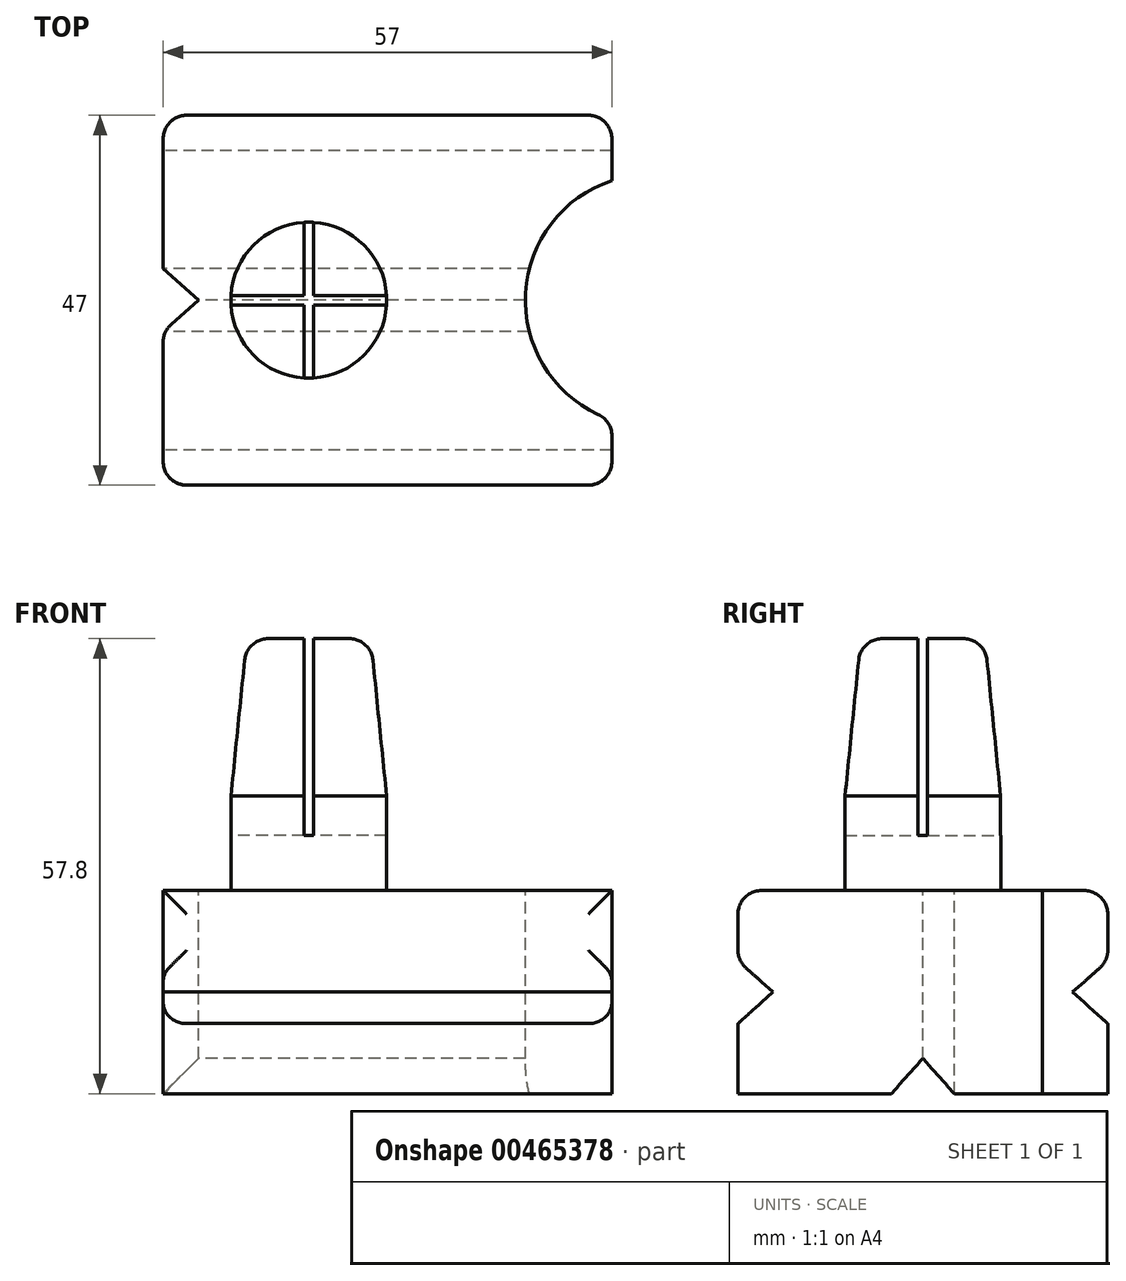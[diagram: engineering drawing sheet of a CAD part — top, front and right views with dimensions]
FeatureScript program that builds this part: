
annotation { "Feature Type Name" : "Feature", "Feature Type Description" : "" }
export const myFeature = defineFeature(function(context is Context, id is Id, definition is map)
    precondition{}
    {
        {
            var Q0;
            Q0=qCreatedBy(makeId("Top.planeOp"),FACE);
            var sketch = newSketch(context, id + "F0", { "sketchPlane" : qUnion([Q0])});
            skLineSegment(sketch, "E0.bottom", {"start": v(18.5, -23.5) * mm, "end": v(-18.5, -23.5) * mm});
            skLineSegment(sketch, "E0.top", {"start": v(18.5, 23.5) * mm, "end": v(-18.5, 23.5) * mm});
            skLineSegment(sketch, "E0.left", {"start": v(18.5, -23.5) * mm, "end": v(18.5, 23.5) * mm});
            skLineSegment(sketch, "E0.right", {"start": v(-18.5, -23.5) * mm, "end": v(-18.5, 23.5) * mm});
            skPoint(sketch, "E0.middle", {"position": v(0, 0) * mm});
            skCircle(sketch, "E1", {"center": v(0, 0) * mm, "radius": 9.9 * mm});
            skSolve(sketch);
        }
        {
            var Q0;
            Q0=makeQuery(id+"F0.imprint","IMPRINT",FACE,{"disambiguationData":[TD([[makeQuery(id+"F0.imprint","IMPRINT",EDGE,{"derivedFrom":sQuery(id+"F0.wireOp",EDGE,"E1")}),1.0]])]});
            extrude(context, id + "F1", {"entities" : qUnion([Q0]), "depth" : 32 * mm});
        }
        {
            var Q0;
            Q0=makeQuery(id+"F0.imprint","IMPRINT",FACE,{"disambiguationData":[TD([[makeQuery(id+"F0.imprint","IMPRINT",EDGE,{"derivedFrom":sQuery(id+"F0.wireOp",EDGE,"E0.bottom")}),-1.0]])]});
            var Q1;
            Q1=makeQuery(id+"F0.imprint","IMPRINT",FACE,{"disambiguationData":[TD([[makeQuery(id+"F0.imprint","IMPRINT",EDGE,{"derivedFrom":sQuery(id+"F0.wireOp",EDGE,"E1")}),1.0]])]});
            extrude(context, id + "F2", {"entities" : qUnion([Q0, Q1]), "operationType" : NewBodyOperationType.ADD, "oppositeDirection" : true, "depth" : 25.8 * mm});
        }
        {
            var Q0;
            Q0=makeQuery(id+"F2.opExtrude","SWEPT_FACE",FACE,{"disambiguationData":[OSD([sQuery(id+"F0.wireOp",EDGE,"E0.left")])]});
            extrude(context, id + "F3", {"entities" : qUnion([Q0]), "operationType" : NewBodyOperationType.ADD, "depth" : 20 * mm});
        }
        {
            var Q0;
            {var subQ0=sQuery(id+"F0.wireOp",EDGE,"E0.left");Q0=makeQuery(id+"F3.boolean.opBoolean","MERGE",FACE,{"derivedFrom":[makeQuery(id+"F2.opExtrude","CAP_FACE",FACE,{"disambiguationData":[OSD([sQuery(id+"F0.wireOp",EDGE,"E0.bottom"),sQuery(id+"F0.wireOp",EDGE,"E0.top"),subQ0,sQuery(id+"F0.wireOp",EDGE,"E0.right")])],"isStart":true}),makeQuery(id+"F3.opExtrude","SWEPT_FACE",FACE,{"disambiguationData":[OSD([subQ0]),TDD([makeQuery(id+"F2.opExtrude","CAP_EDGE",EDGE,{"disambiguationData":[OSD([subQ0])],"isStart":true})])]})]});}
            var sketch = newSketch(context, id + "F4", { "sketchPlane" : qUnion([Q0])});
            skCircle(sketch, "E2", {"center": v(43.5, 0) * mm, "radius": 16 * mm});
            skSolve(sketch);
        }
        {
            var Q0;
            Q0=makeQuery(id+"F1.opExtrude","CAP_EDGE",EDGE,{"disambiguationData":[OSD([sQuery(id+"F0.wireOp",EDGE,"E1")])],"isStart":false});
            chamfer(context, id + "F5", {"entities" : qUnion([Q0]), "chamferType" : ChamferType.TWO_OFFSETS, "width1" : 2 * mm, "oppositeDirection" : false, "width2" : 20 * mm, "tangentPropagation" : true});
        }
        {
            var Q0;
            {var subQ0=sQuery(id+"F4.wireOp",EDGE,"E2");var subQ1=sQuery(id+"F0.wireOp",EDGE,"E0.left");var subQ2=makeQuery(id+"F3.opExtrude","CAP_EDGE",EDGE,{"disambiguationData":[OSD([subQ1]),TDD([makeQuery(id+"F2.opExtrude","CAP_EDGE",EDGE,{"disambiguationData":[OSD([subQ1])],"isStart":true})])],"isStart":false});var subQ3=makeQuery(id+"F4.imprint","INTERSECT",VERTEX,{"disambiguationData":[OD(0.0)],"derivedFrom":[subQ2,subQ0]});Q0=makeQuery(id+"F4.imprint","IMPRINT",FACE,{"disambiguationData":[TD([[makeQuery(id+"F4.imprint","IMPRINT",EDGE,{"disambiguationData":[TD([[subQ3,1.0]])],"derivedFrom":subQ0}),1.0]])]});}
            extrude(context, id + "F6", {"entities" : qUnion([Q0]), "operationType" : NewBodyOperationType.REMOVE, "endBound" : BoundingType.THROUGH_ALL, "oppositeDirection" : true, "depth" : 25 * mm});
        }
        {
            var Q0;
            {var subQ1=sQuery(id+"F0.wireOp",EDGE,"E0.top");var subQ2=sQuery(id+"F0.wireOp",EDGE,"E0.right");Q0=makeQuery(id+"FCS6urC5TY2NgVd_1.boolean.opBoolean","SPLIT",FACE,{"disambiguationData":[TD([makeQuery(id+"F2.opExtrude","SWEPT_FACE",FACE,{"disambiguationData":[OSD([subQ1])]})])],"derivedFrom":makeQuery(id+"F2.opExtrude","SWEPT_FACE",FACE,{"disambiguationData":[OSD([subQ2])]})});}
            var sketch = newSketch(context, id + "F7", { "sketchPlane" : qUnion([Q0])});
            skLineSegment(sketch, "E3", {"start": v(-23.5, -12.9) * mm, "end": v(23.5, -12.9) * mm, "construction": true});
            skLineSegment(sketch, "E4", {"start": v(-19.03, -12.9) * mm, "end": v(-23.5, -16.9) * mm});
            skLineSegment(sketch, "E5", {"start": v(-23.5, -16.9) * mm, "end": v(-23.5, -8.9) * mm});
            skLineSegment(sketch, "E6", {"start": v(-23.5, -8.9) * mm, "end": v(-19.03, -12.9) * mm});
            skLineSegment(sketch, "E7.MirrorCS", {"start": v(23.5, -16.9) * mm, "end": v(23.5, -8.9) * mm});
            skLineSegment(sketch, "E8.MirrorCS", {"start": v(23.5, -8.9) * mm, "end": v(19.03, -12.9) * mm});
            skLineSegment(sketch, "E9.MirrorCS", {"start": v(19.03, -12.9) * mm, "end": v(23.5, -16.9) * mm});
            skSolve(sketch);
        }
        {
            var Q0;
            Q0=makeQuery(id+"F7.imprint","IMPRINT",FACE,{"disambiguationData":[TD([[makeQuery(id+"F7.imprint","IMPRINT",EDGE,{"derivedFrom":sQuery(id+"F7.wireOp",EDGE,"E4")}),-1.0]])]});
            var Q1;
            Q1=makeQuery(id+"F7.imprint","IMPRINT",FACE,{"disambiguationData":[TD([[makeQuery(id+"F7.imprint","IMPRINT",EDGE,{"derivedFrom":sQuery(id+"F7.wireOp",EDGE,"E7.MirrorCS")}),1.0]])]});
            extrude(context, id + "F8", {"entities" : qUnion([Q0, Q1]), "operationType" : NewBodyOperationType.REMOVE, "endBound" : BoundingType.THROUGH_ALL, "oppositeDirection" : true, "depth" : 25 * mm});
        }
        {
            var Q0;
            Q0=makeQuery(id+"F0.imprint","IMPRINT",FACE,{"disambiguationData":[TD([[makeQuery(id+"F0.imprint","IMPRINT",EDGE,{"derivedFrom":sQuery(id+"F0.wireOp",EDGE,"E0.bottom")}),-1.0]])]});
            var sketch = newSketch(context, id + "F9", { "sketchPlane" : qUnion([Q0])});
            skLineSegment(sketch, "E10", {"start": v(-14.03, 0) * mm, "end": v(-18.5, 4) * mm});
            skLineSegment(sketch, "E11", {"start": v(-18.5, 4) * mm, "end": v(-18.5, -4) * mm});
            skLineSegment(sketch, "E12", {"start": v(-18.5, -4) * mm, "end": v(-14.03, 0) * mm});
            skSolve(sketch);
        }
        {
            var Q0;
            Q0=makeQuery(id+"F2.opExtrude","SWEPT_FACE",FACE,{"disambiguationData":[OSD([sQuery(id+"F0.wireOp",EDGE,"E0.right")])]});
            var sketch = newSketch(context, id + "F10", { "sketchPlane" : qUnion([Q0])});
            skLineSegment(sketch, "E13", {"start": v(0, -21.33) * mm, "end": v(-4, -25.8) * mm});
            skLineSegment(sketch, "E14", {"start": v(-4, -25.8) * mm, "end": v(4, -25.8) * mm});
            skLineSegment(sketch, "E15", {"start": v(4, -25.8) * mm, "end": v(0, -21.33) * mm});
            skSolve(sketch);
        }
        {
            var Q0;
            Q0=qSketchRegion(id+"F10",true);
            extrude(context, id + "F11", {"entities" : qUnion([Q0]), "operationType" : NewBodyOperationType.REMOVE, "endBound" : BoundingType.THROUGH_ALL, "oppositeDirection" : true, "depth" : 25 * mm});
        }
        {
            var Q0;
            Q0=makeQuery(id+"F9.imprint","IMPRINT",FACE,{"disambiguationData":[TD([[makeQuery(id+"F9.imprint","IMPRINT",EDGE,{"derivedFrom":sQuery(id+"F9.wireOp",EDGE,"E10")}),1.0]])]});
            extrude(context, id + "F12", {"entities" : qUnion([Q0]), "operationType" : NewBodyOperationType.REMOVE, "endBound" : BoundingType.THROUGH_ALL, "oppositeDirection" : true, "depth" : 25 * mm});
        }
        {
            var Q0;
            Q0=makeQuery(id+"F1.opExtrude","CAP_FACE",FACE,{"disambiguationData":[OSD([sQuery(id+"F0.wireOp",EDGE,"E1")])],"isStart":false});
            var sketch = newSketch(context, id + "F13", { "sketchPlane" : qUnion([Q0])});
            skLineSegment(sketch, "E16.bottom", {"start": v(0.6, -10.5) * mm, "end": v(-0.6, -10.5) * mm});
            skLineSegment(sketch, "E16.top", {"start": v(0.6, 10.5) * mm, "end": v(-0.6, 10.5) * mm});
            skLineSegment(sketch, "E16.left", {"start": v(0.6, -10.5) * mm, "end": v(0.6, 10.5) * mm});
            skLineSegment(sketch, "E16.right", {"start": v(-0.6, -10.5) * mm, "end": v(-0.6, 10.5) * mm});
            skPoint(sketch, "E16.middle", {"position": v(0, 0) * mm});
            skLineSegment(sketch, "E17.bottom", {"start": v(10.5, -0.6) * mm, "end": v(-10.5, -0.6) * mm});
            skLineSegment(sketch, "E17.top", {"start": v(10.5, 0.6) * mm, "end": v(-10.5, 0.6) * mm});
            skLineSegment(sketch, "E17.left", {"start": v(10.5, -0.6) * mm, "end": v(10.5, 0.6) * mm});
            skLineSegment(sketch, "E17.right", {"start": v(-10.5, -0.6) * mm, "end": v(-10.5, 0.6) * mm});
            skSolve(sketch);
        }
        {
            var Q0;
            Q0=qSketchRegion(id+"F13",true);
            extrude(context, id + "F14", {"entities" : qUnion([Q0]), "operationType" : NewBodyOperationType.REMOVE, "oppositeDirection" : true, "depth" : 25 * mm});
        }
        {
            var Q0;
            {var subQ0=sQuery(id+"F0.wireOp",EDGE,"E0.right");var subQ2=sQuery(id+"F0.wireOp",EDGE,"E0.top");Q0=makeQuery(id+"F8.boolean.opBoolean","SPLIT",EDGE,{"disambiguationData":[TD([makeQuery(id+"F8.opExtrude","SWEPT_FACE",FACE,{"disambiguationData":[OSD([sQuery(id+"F7.wireOp",EDGE,"E6")])]})])],"derivedFrom":makeQuery(id+"F2.opExtrude","SWEPT_EDGE",EDGE,{"disambiguationData":[OSD([subQ2,subQ0])]})});}
            var Q1;
            {var subQ0=sQuery(id+"F0.wireOp",EDGE,"E0.right");var subQ2=sQuery(id+"F0.wireOp",EDGE,"E0.top");Q1=makeQuery(id+"F8.boolean.opBoolean","SPLIT",EDGE,{"disambiguationData":[TD([makeQuery(id+"F8.opExtrude","SWEPT_FACE",FACE,{"disambiguationData":[OSD([sQuery(id+"F7.wireOp",EDGE,"E4")])]})])],"derivedFrom":makeQuery(id+"F2.opExtrude","SWEPT_EDGE",EDGE,{"disambiguationData":[OSD([subQ2,subQ0])]})});}
            var Q2;
            {var subQ1=sQuery(id+"F0.wireOp",EDGE,"E0.bottom");var subQ2=sQuery(id+"F0.wireOp",EDGE,"E0.right");Q2=makeQuery(id+"F8.boolean.opBoolean","SPLIT",EDGE,{"disambiguationData":[TD([makeQuery(id+"F8.opExtrude","SWEPT_FACE",FACE,{"disambiguationData":[OSD([sQuery(id+"F7.wireOp",EDGE,"E8.MirrorCS")])]})])],"derivedFrom":makeQuery(id+"F2.opExtrude","SWEPT_EDGE",EDGE,{"disambiguationData":[OSD([subQ1,subQ2])]})});}
            var Q3;
            {var subQ1=sQuery(id+"F0.wireOp",EDGE,"E0.bottom");var subQ2=sQuery(id+"F0.wireOp",EDGE,"E0.right");Q3=makeQuery(id+"F8.boolean.opBoolean","SPLIT",EDGE,{"disambiguationData":[TD([makeQuery(id+"F8.opExtrude","SWEPT_FACE",FACE,{"disambiguationData":[OSD([sQuery(id+"F7.wireOp",EDGE,"E9.MirrorCS")])]})])],"derivedFrom":makeQuery(id+"F2.opExtrude","SWEPT_EDGE",EDGE,{"disambiguationData":[OSD([subQ1,subQ2])]})});}
            var Q4;
            {var subQ0=sQuery(id+"F0.wireOp",EDGE,"E0.left");var subQ1=sQuery(id+"F0.wireOp",EDGE,"E0.bottom");Q4=makeQuery(id+"F8.boolean.opBoolean","SPLIT",EDGE,{"disambiguationData":[TD([makeQuery(id+"F8.opExtrude","SWEPT_FACE",FACE,{"disambiguationData":[OSD([sQuery(id+"F7.wireOp",EDGE,"E8.MirrorCS")])]})])],"derivedFrom":makeQuery(id+"F3.opExtrude","CAP_EDGE",EDGE,{"disambiguationData":[OSD([subQ1,subQ0])],"isStart":false})});}
            var Q5;
            {var subQ0=sQuery(id+"F0.wireOp",EDGE,"E0.left");var subQ1=sQuery(id+"F0.wireOp",EDGE,"E0.bottom");Q5=makeQuery(id+"F8.boolean.opBoolean","SPLIT",EDGE,{"disambiguationData":[TD([makeQuery(id+"F8.opExtrude","SWEPT_FACE",FACE,{"disambiguationData":[OSD([sQuery(id+"F7.wireOp",EDGE,"E9.MirrorCS")])]})])],"derivedFrom":makeQuery(id+"F3.opExtrude","CAP_EDGE",EDGE,{"disambiguationData":[OSD([subQ1,subQ0])],"isStart":false})});}
            var Q6;
            {var subQ0=sQuery(id+"F4.wireOp",EDGE,"E2");var subQ1=sQuery(id+"F0.wireOp",EDGE,"E0.left");Q6=makeQuery(id+"F6.boolean.opBoolean","COPY",EDGE,{"derivedFrom":makeQuery(id+"F6.opExtrude","SWEPT_EDGE",EDGE,{"disambiguationData":[OSD([subQ1,subQ0]),TDD([makeQuery(id+"F4.imprint","INTERSECT",VERTEX,{"disambiguationData":[OD(1.0)],"derivedFrom":[makeQuery(id+"F3.opExtrude","CAP_EDGE",EDGE,{"disambiguationData":[OSD([subQ1]),TDD([makeQuery(id+"F2.opExtrude","CAP_EDGE",EDGE,{"disambiguationData":[OSD([subQ1])],"isStart":true})])],"isStart":false}),subQ0]})])]})});}
            var Q7;
            {var subQ0=sQuery(id+"F4.wireOp",EDGE,"E2");var subQ1=sQuery(id+"F0.wireOp",EDGE,"E0.left");Q7=makeQuery(id+"F6.boolean.opBoolean","COPY",EDGE,{"derivedFrom":makeQuery(id+"F6.opExtrude","SWEPT_EDGE",EDGE,{"disambiguationData":[OSD([subQ1,subQ0]),TDD([makeQuery(id+"F4.imprint","INTERSECT",VERTEX,{"disambiguationData":[OD(0.0)],"derivedFrom":[makeQuery(id+"F3.opExtrude","CAP_EDGE",EDGE,{"disambiguationData":[OSD([subQ1]),TDD([makeQuery(id+"F2.opExtrude","CAP_EDGE",EDGE,{"disambiguationData":[OSD([subQ1])],"isStart":true})])],"isStart":false}),subQ0]})])]})});}
            var Q8;
            {var subQ0=sQuery(id+"F0.wireOp",EDGE,"E0.left");var subQ1=sQuery(id+"F0.wireOp",EDGE,"E0.top");Q8=makeQuery(id+"F8.boolean.opBoolean","SPLIT",EDGE,{"disambiguationData":[TD([makeQuery(id+"F8.opExtrude","SWEPT_FACE",FACE,{"disambiguationData":[OSD([sQuery(id+"F7.wireOp",EDGE,"E6")])]})])],"derivedFrom":makeQuery(id+"F3.opExtrude","CAP_EDGE",EDGE,{"disambiguationData":[OSD([subQ1,subQ0])],"isStart":false})});}
            var Q9;
            {var subQ0=sQuery(id+"F0.wireOp",EDGE,"E0.left");var subQ1=sQuery(id+"F0.wireOp",EDGE,"E0.top");Q9=makeQuery(id+"F8.boolean.opBoolean","SPLIT",EDGE,{"disambiguationData":[TD([makeQuery(id+"F8.opExtrude","SWEPT_FACE",FACE,{"disambiguationData":[OSD([sQuery(id+"F7.wireOp",EDGE,"E4")])]})])],"derivedFrom":makeQuery(id+"F3.opExtrude","CAP_EDGE",EDGE,{"disambiguationData":[OSD([subQ1,subQ0])],"isStart":false})});}
            var Q10;
            {var subQ0=sQuery(id+"F0.wireOp",EDGE,"E0.left");var subQ1=sQuery(id+"F0.wireOp",EDGE,"E0.bottom");Q10=makeQuery(id+"F3.boolean.opBoolean","MERGE",EDGE,{"derivedFrom":[makeQuery(id+"F2.opExtrude","CAP_EDGE",EDGE,{"disambiguationData":[OSD([subQ1])],"isStart":true}),makeQuery(id+"F3.opExtrude","SWEPT_EDGE",EDGE,{"disambiguationData":[OSD([subQ1,subQ0]),TDD([makeQuery(id+"F2.opExtrude","CAP_VERTEX",VERTEX,{"disambiguationData":[OSD([subQ1,subQ0])],"isStart":true})])]})]});}
            var Q11;
            {var subQ0=sQuery(id+"F0.wireOp",EDGE,"E0.left");var subQ1=sQuery(id+"F0.wireOp",EDGE,"E0.top");Q11=makeQuery(id+"F3.boolean.opBoolean","MERGE",EDGE,{"derivedFrom":[makeQuery(id+"F2.opExtrude","CAP_EDGE",EDGE,{"disambiguationData":[OSD([subQ1])],"isStart":true}),makeQuery(id+"F3.opExtrude","SWEPT_EDGE",EDGE,{"disambiguationData":[OSD([subQ1,subQ0]),TDD([makeQuery(id+"F2.opExtrude","CAP_VERTEX",VERTEX,{"disambiguationData":[OSD([subQ1,subQ0])],"isStart":true})])]})]});}
            var Q12;
            Q12=makeQuery(id+"F8.boolean.opBoolean","COPY",EDGE,{"derivedFrom":makeQuery(id+"F8.opExtrude","SWEPT_EDGE",EDGE,{"disambiguationData":[OSD([sQuery(id+"F0.wireOp",EDGE,"E0.top"),sQuery(id+"F0.wireOp",EDGE,"E0.right"),sQuery(id+"F7.wireOp",EDGE,"E4"),sQuery(id+"F7.wireOp",EDGE,"E5")])]})});
            var Q13;
            Q13=makeQuery(id+"F8.boolean.opBoolean","COPY",EDGE,{"derivedFrom":makeQuery(id+"F8.opExtrude","SWEPT_EDGE",EDGE,{"disambiguationData":[OSD([sQuery(id+"F0.wireOp",EDGE,"E0.bottom"),sQuery(id+"F0.wireOp",EDGE,"E0.right"),sQuery(id+"F7.wireOp",EDGE,"E7.MirrorCS"),sQuery(id+"F7.wireOp",EDGE,"E8.MirrorCS")])]})});
            var Q14;
            Q14=makeQuery(id+"F8.boolean.opBoolean","COPY",EDGE,{"derivedFrom":makeQuery(id+"F8.opExtrude","SWEPT_EDGE",EDGE,{"disambiguationData":[OSD([sQuery(id+"F0.wireOp",EDGE,"E0.bottom"),sQuery(id+"F0.wireOp",EDGE,"E0.right"),sQuery(id+"F7.wireOp",EDGE,"E7.MirrorCS"),sQuery(id+"F7.wireOp",EDGE,"E9.MirrorCS")])]})});
            var Q15;
            Q15=makeQuery(id+"F8.boolean.opBoolean","COPY",EDGE,{"derivedFrom":makeQuery(id+"F8.opExtrude","SWEPT_EDGE",EDGE,{"disambiguationData":[OSD([sQuery(id+"F0.wireOp",EDGE,"E0.top"),sQuery(id+"F0.wireOp",EDGE,"E0.right"),sQuery(id+"F7.wireOp",EDGE,"E5"),sQuery(id+"F7.wireOp",EDGE,"E6")])]})});
            var Q16;
            Q16=makeQuery(id+"F12.boolean.opBoolean","COPY",EDGE,{"derivedFrom":makeQuery(id+"F12.opExtrude","SWEPT_EDGE",EDGE,{"disambiguationData":[OSD([sQuery(id+"F0.wireOp",EDGE,"E0.right"),sQuery(id+"F9.wireOp",EDGE,"E10"),sQuery(id+"F9.wireOp",EDGE,"E11")])]})});
            var Q17;
            Q17=makeQuery(id+"F12.boolean.opBoolean","COPY",EDGE,{"derivedFrom":makeQuery(id+"F12.opExtrude","SWEPT_EDGE",EDGE,{"disambiguationData":[OSD([sQuery(id+"F0.wireOp",EDGE,"E0.right"),sQuery(id+"F9.wireOp",EDGE,"E11"),sQuery(id+"F9.wireOp",EDGE,"E12")])]})});
            var Q18;
            {var subQ0=sQuery(id+"F0.wireOp",EDGE,"E1");var subQ1=makeQuery(id+"F1.opExtrude","CAP_FACE",FACE,{"disambiguationData":[OSD([subQ0])],"isStart":false});var subQ2=sQuery(id+"F13.wireOp",EDGE,"E16.right");var subQ3=makeQuery(id+"F5.opChamfer","BLEND_EDGE",EDGE,{"blendedFrom":[makeQuery(id+"F1.opExtrude","CAP_EDGE",EDGE,{"disambiguationData":[OSD([subQ0])],"isStart":false}),subQ1],"blendedInto":[subQ1]});var subQ5=sQuery(id+"F13.wireOp",EDGE,"E17.top");var subQ6=makeQuery(id+"F13.imprint","INTERSECT",VERTEX,{"derivedFrom":[subQ2,subQ5]});Q18=makeQuery(id+"F14.boolean.opBoolean","SPLIT",EDGE,{"disambiguationData":[TD([makeQuery(id+"F14.opExtrude","SWEPT_FACE",FACE,{"disambiguationData":[OSD([subQ2]),TDD([makeQuery(id+"F13.imprint","IMPRINT",EDGE,{"disambiguationData":[TD([[subQ6,-1.0]])],"derivedFrom":subQ2}),makeQuery(id+"F13.imprint","IMPRINT",EDGE,{"disambiguationData":[TD([[makeQuery(id+"F13.imprint","INTERSECT",VERTEX,{"derivedFrom":[sQuery(id+"F13.wireOp",EDGE,"E16.top"),subQ2]}),1.0]])],"derivedFrom":subQ2})])]})])],"derivedFrom":subQ3});}
            var Q19;
            {var subQ0=sQuery(id+"F0.wireOp",EDGE,"E1");var subQ1=makeQuery(id+"F1.opExtrude","CAP_FACE",FACE,{"disambiguationData":[OSD([subQ0])],"isStart":false});var subQ2=sQuery(id+"F13.wireOp",EDGE,"E17.bottom");var subQ3=sQuery(id+"F13.wireOp",EDGE,"E16.right");var subQ4=makeQuery(id+"F13.imprint","INTERSECT",VERTEX,{"derivedFrom":[subQ3,subQ2]});var subQ5=makeQuery(id+"F5.opChamfer","BLEND_EDGE",EDGE,{"blendedFrom":[makeQuery(id+"F1.opExtrude","CAP_EDGE",EDGE,{"disambiguationData":[OSD([subQ0])],"isStart":false}),subQ1],"blendedInto":[subQ1]});Q19=makeQuery(id+"F14.boolean.opBoolean","SPLIT",EDGE,{"disambiguationData":[TD([makeQuery(id+"F14.opExtrude","SWEPT_FACE",FACE,{"disambiguationData":[OSD([subQ3]),TDD([makeQuery(id+"F13.imprint","IMPRINT",EDGE,{"disambiguationData":[TD([[makeQuery(id+"F13.imprint","INTERSECT",VERTEX,{"derivedFrom":[sQuery(id+"F13.wireOp",EDGE,"E16.bottom"),subQ3]}),-1.0]])],"derivedFrom":subQ3}),makeQuery(id+"F13.imprint","IMPRINT",EDGE,{"disambiguationData":[TD([[subQ4,1.0]])],"derivedFrom":subQ3})])]})])],"derivedFrom":subQ5});}
            var Q20;
            {var subQ0=sQuery(id+"F0.wireOp",EDGE,"E1");var subQ1=makeQuery(id+"F1.opExtrude","CAP_FACE",FACE,{"disambiguationData":[OSD([subQ0])],"isStart":false});var subQ2=sQuery(id+"F13.wireOp",EDGE,"E17.bottom");var subQ3=sQuery(id+"F13.wireOp",EDGE,"E16.left");var subQ4=makeQuery(id+"F13.imprint","INTERSECT",VERTEX,{"derivedFrom":[subQ3,subQ2]});var subQ5=makeQuery(id+"F5.opChamfer","BLEND_EDGE",EDGE,{"blendedFrom":[makeQuery(id+"F1.opExtrude","CAP_EDGE",EDGE,{"disambiguationData":[OSD([subQ0])],"isStart":false}),subQ1],"blendedInto":[subQ1]});Q20=makeQuery(id+"F14.boolean.opBoolean","SPLIT",EDGE,{"disambiguationData":[TD([makeQuery(id+"F14.opExtrude","SWEPT_FACE",FACE,{"disambiguationData":[OSD([subQ3]),TDD([makeQuery(id+"F13.imprint","IMPRINT",EDGE,{"disambiguationData":[TD([[makeQuery(id+"F13.imprint","INTERSECT",VERTEX,{"derivedFrom":[sQuery(id+"F13.wireOp",EDGE,"E16.bottom"),subQ3]}),-1.0]])],"derivedFrom":subQ3}),makeQuery(id+"F13.imprint","IMPRINT",EDGE,{"disambiguationData":[TD([[subQ4,1.0]])],"derivedFrom":subQ3})])]})])],"derivedFrom":subQ5});}
            var Q21;
            {var subQ0=sQuery(id+"F0.wireOp",EDGE,"E1");var subQ1=makeQuery(id+"F1.opExtrude","CAP_FACE",FACE,{"disambiguationData":[OSD([subQ0])],"isStart":false});var subQ2=sQuery(id+"F13.wireOp",EDGE,"E16.left");var subQ3=makeQuery(id+"F5.opChamfer","BLEND_EDGE",EDGE,{"blendedFrom":[makeQuery(id+"F1.opExtrude","CAP_EDGE",EDGE,{"disambiguationData":[OSD([subQ0])],"isStart":false}),subQ1],"blendedInto":[subQ1]});var subQ5=sQuery(id+"F13.wireOp",EDGE,"E17.top");var subQ6=makeQuery(id+"F13.imprint","INTERSECT",VERTEX,{"derivedFrom":[subQ2,subQ5]});Q21=makeQuery(id+"F14.boolean.opBoolean","SPLIT",EDGE,{"disambiguationData":[TD([makeQuery(id+"F14.opExtrude","SWEPT_FACE",FACE,{"disambiguationData":[OSD([subQ2]),TDD([makeQuery(id+"F13.imprint","IMPRINT",EDGE,{"disambiguationData":[TD([[subQ6,-1.0]])],"derivedFrom":subQ2}),makeQuery(id+"F13.imprint","IMPRINT",EDGE,{"disambiguationData":[TD([[makeQuery(id+"F13.imprint","INTERSECT",VERTEX,{"derivedFrom":[sQuery(id+"F13.wireOp",EDGE,"E16.top"),subQ2]}),1.0]])],"derivedFrom":subQ2})])]})])],"derivedFrom":subQ3});}
            fillet(context, id + "F15", {"entities" : qUnion([Q0, Q1, Q2, Q3, Q4, Q5, Q6, Q7, Q8, Q9, Q10, Q11, Q12, Q13, Q14, Q15, Q16, Q17, Q18, Q19, Q20, Q21]), "radius" : 3 * mm, "tangentPropagation" : true, "allowEdgeOverflow" : false});
        }
    });
